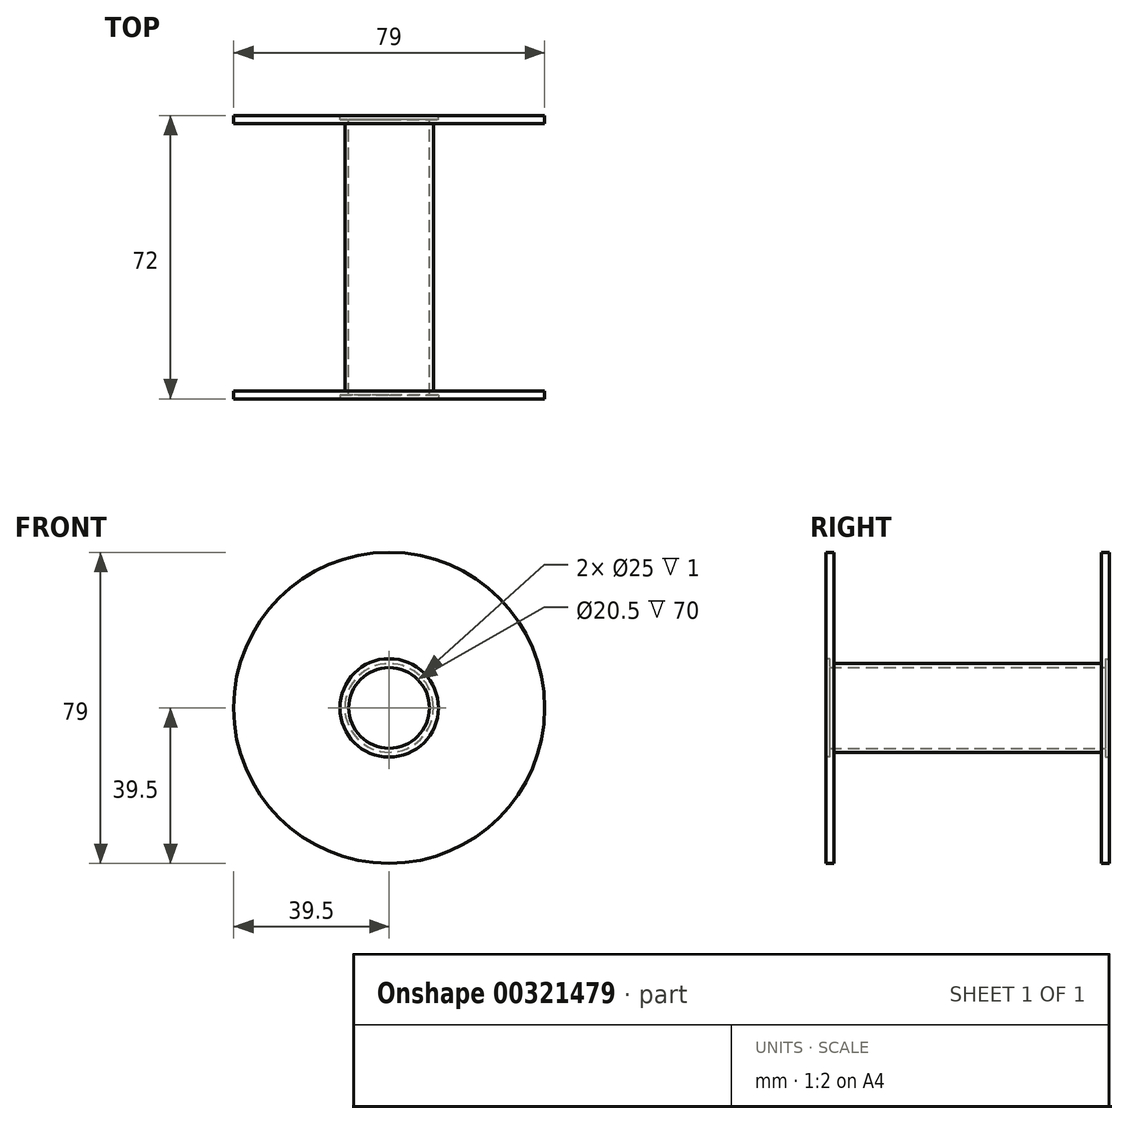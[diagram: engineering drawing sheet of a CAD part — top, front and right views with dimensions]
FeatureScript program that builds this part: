
annotation { "Feature Type Name" : "Feature", "Feature Type Description" : "" }
export const myFeature = defineFeature(function(context is Context, id is Id, definition is map)
    precondition{}
    {
        {
            var Q0;
            Q0=qCreatedBy(makeId("Front.planeOp"),FACE);
            var sketch = newSketch(context, id + "F0", { "sketchPlane" : qUnion([Q0])});
            skCircle(sketch, "E0", {"center": v(0, 0) * mm, "radius": 10.25 * mm});
            skCircle(sketch, "E1", {"center": v(0, 0) * mm, "radius": 39.5 * mm});
            skSolve(sketch);
        }
        {
            var Q0;
            Q0 = qSketchRegion(id + "F0", true);
            extrude(context, id + "F1", {"entities" : qUnion([Q0]), "depth" : 2 * mm});
        }
        {
            var Q0;
            Q0=makeQuery(id+"F1.opExtrude","CAP_FACE",FACE,{"disambiguationData":[OSD([sQuery(id+"F0.wireOp",EDGE,"E0"),sQuery(id+"F0.wireOp",EDGE,"E1")])],"isStart":false});
            var sketch = newSketch(context, id + "F2", { "sketchPlane" : qUnion([Q0])});
            skCircle(sketch, "E2", {"center": v(0, 0) * mm, "radius": 10.25 * mm});
            skCircle(sketch, "E3", {"center": v(0, 0) * mm, "radius": 11.25 * mm});
            skSolve(sketch);
        }
        {
            var Q0;
            Q0 = qSketchRegion(id + "F2", true);
            extrude(context, id + "F3", {"entities" : qUnion([Q0]), "operationType" : NewBodyOperationType.ADD, "depth" : 68 * mm});
        }
        {
            var Q0;
            Q0=makeQuery(id+"F1.opExtrude","CAP_FACE",FACE,{"disambiguationData":[OSD([sQuery(id+"F0.wireOp",EDGE,"E0"),sQuery(id+"F0.wireOp",EDGE,"E1")])],"isStart":true});
            var sketch = newSketch(context, id + "F4", { "sketchPlane" : qUnion([Q0])});
            skCircle(sketch, "E4", {"center": v(0, 0) * mm, "radius": 12.5 * mm});
            skSolve(sketch);
        }
        {
            var Q0;
            Q0 = qSketchRegion(id + "F4", true);
            extrude(context, id + "F5", {"entities" : qUnion([Q0]), "operationType" : NewBodyOperationType.REMOVE, "oppositeDirection" : true, "depth" : 1 * mm});
        }
        {
            var Q0;
            Q0=makeQuery(id+"F3.opExtrude","CAP_FACE",FACE,{"disambiguationData":[OSD([sQuery(id+"F2.wireOp",EDGE,"E2"),sQuery(id+"F2.wireOp",EDGE,"E3")])],"isStart":false});
            var sketch = newSketch(context, id + "F6", { "sketchPlane" : qUnion([Q0])});
            skCircle(sketch, "E5", {"center": v(0, 0) * mm, "radius": 10.25 * mm});
            skCircle(sketch, "E6", {"center": v(0, 0) * mm, "radius": 39.5 * mm});
            skSolve(sketch);
        }
        {
            var Q0;
            Q0 = qSketchRegion(id + "F6", true);
            extrude(context, id + "F7", {"entities" : qUnion([Q0]), "operationType" : NewBodyOperationType.ADD, "depth" : 2 * mm});
        }
        {
            var Q0;
            Q0=makeQuery(id+"F7.opExtrude","CAP_FACE",FACE,{"disambiguationData":[OSD([sQuery(id+"F6.wireOp",EDGE,"E5"),sQuery(id+"F6.wireOp",EDGE,"E6")])],"isStart":false});
            var sketch = newSketch(context, id + "F8", { "sketchPlane" : qUnion([Q0])});
            skCircle(sketch, "E7", {"center": v(0, 0) * mm, "radius": 12.5 * mm});
            skSolve(sketch);
        }
        {
            var Q0;
            Q0 = qSketchRegion(id + "F8", true);
            extrude(context, id + "F9", {"entities" : qUnion([Q0]), "operationType" : NewBodyOperationType.REMOVE, "oppositeDirection" : true, "depth" : 1 * mm});
        }
    });
